# Revit family: Electrical-Box_FSR_WBPS
name_source: partatom
category: Electrical Fixtures
units: mm (PartAtom-declared; Revit-internal decimal feet)

## family parameters
Always vertical = Yes
Classification Number = 23.85.10.17.11
Cut with Voids When Loaded = No
Host = Wall
Maintain Annotation Orientation = No
Part Type = Normal
Room Calculation Point = No
Round Connector Dimension = Use Diameter
Shared = No

## types (4) — shared parameters
Assembly Code = D5020100
Body Material = Material and Finish as Specified in 26 27 26
Building Codes = ftp://doclib.fsrinc.com/
Construction Details = ftp://doclib.fsrinc.com/
Cover Material = Material and Finish as Specified in 26 27 26
Default Elevation = 0"
Description = Electrical Box as Specified in 26 27 26
Full Height = 6 49/256"
Glazing = Translucent Plastic
Green Building-LEED = http://www.arcat.com
Gross Depth = 3"
Gross Height = 4 1/4"
Gross Projection = 1 41/256"
Installation-Fabrication = ftp://doclib.fsrinc.com/
Keynote = 26 27 26
Manufacturer = FSR Inc.
Manufacturer Fax = 973-785-4207
Manufacturer Website = http://www.fsrinc.com
Model = As Specified in 26 27 26
Product Data = http://www.arcat.com
Sales Information = http://www.fsrinc.com
Specification = http://www.arcat.com
Test Data = ftp://doclib.fsrinc.com/
Trim Material = Material and Finish as Specified in 26 27 26
URL = http://www.fsrinc.com
zero-valued in all types: Expected Lifespan (Years), Maintenance Schedule (Months), Warranty Duration (Years)

## per-type parameters (varying)
| type | Full Width | Gross Width | Window Width |
| WB-PS5G | 11 159/256" | 10 1/4" | 9 11/16" |
| WB-PS4G | 9 207/256" | 8 1/4" | 7 7/8" |
| WB-PS3G | 8" | 6 1/4" | 6 15/256" |
| WB-PS2G | 6 49/256" | 4 1/4" | 4 1/4" |

## geometry (parser evidence)
native form markers: Sweep x4
no freeform markers — native parametric forms only
